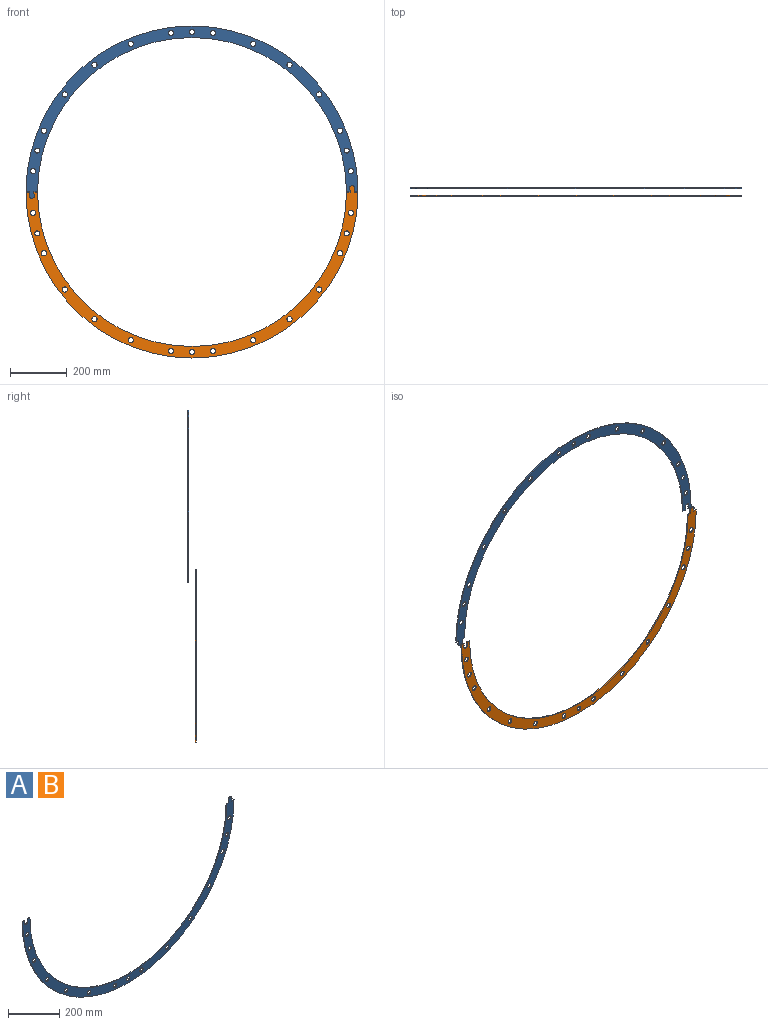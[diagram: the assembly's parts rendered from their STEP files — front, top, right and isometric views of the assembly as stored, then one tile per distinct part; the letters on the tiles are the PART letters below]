
ASSEMBLY  parts=2 mates=1
PART A: 29 faces, bbox 1170.9x3.2x607.7 mm
  f0: plane 12.56x3.18mm, normal (0,0,1), area 39.9mm2, adj f1,f9,f10,f25
  f1: plane 1170.94x607.7mm, normal (0,1,0), area 68201.3mm2, adj f0,f2,f3,f4,f5,f6,f7,f8
  f2: plane 12.84x3.18mm, normal (0,0,1), area 40.8mm2, adj f1,f3,f10,f23
  f3: cylinder r=585.47mm len=1170.94mm, axis (0,1,0), area 5838.2mm2, adj f1,f2,f4,f10
  f4: plane 12.84x3.18mm, normal (0,0,1), area 40.8mm2, adj f1,f3,f5,f10
  f5: plane 7.24x3.18mm, normal (1,0,0), area 23mm2, adj f1,f4,f6,f10
  f6: cylinder r=9.53mm len=19.05mm, axis (0,1,0), area 133.9mm2, adj f1,f5,f7,f10
  f7: plane 7.24x3.18mm, normal (-1,0,0), area 23mm2, adj f1,f6,f8,f10
  f8: plane 12.56x3.18mm, normal (0,0,1), area 39.9mm2, adj f1,f7,f9,f10
  f9: cylinder r=544.83mm len=1089.66mm, axis (0,1,0), area 5432.8mm2, adj f0,f1,f8,f10
  f10: plane 1170.94x607.7mm, normal (0,-1,0), area 68201.3mm2, adj f0,f2,f3,f4,f5,f6,f7,f8
  f11: cylinder r=9.21mm len=18.42mm, axis (0,-1,0), area 183.7mm2, adj f1,f10
  f12: cylinder r=9.21mm len=18.42mm, axis (0,-1,0), area 183.7mm2, adj f1,f10
  f13: cylinder r=9.21mm len=18.42mm, axis (0,-1,0), area 183.7mm2, adj f1,f10
  f14: cylinder r=9.21mm len=18.42mm, axis (0,-1,0), area 183.7mm2, adj f1,f10
  f15: cylinder r=9.21mm len=18.42mm, axis (0,-1,0), area 183.7mm2, adj f1,f10
  f16: cylinder r=9.21mm len=18.42mm, axis (0,-1,0), area 183.7mm2, adj f1,f10
  f17: cylinder r=9.21mm len=18.42mm, axis (0,-1,0), area 183.7mm2, adj f1,f10
  f18: cylinder r=9.21mm len=18.42mm, axis (0,-1,0), area 183.7mm2, adj f1,f10
  f19: cylinder r=9.21mm len=18.42mm, axis (0,-1,0), area 183.7mm2, adj f1,f10
  f20: cylinder r=9.21mm len=18.42mm, axis (0,-1,0), area 183.7mm2, adj f1,f10
  f21: cylinder r=9.21mm len=18.42mm, axis (0,-1,0), area 183.7mm2, adj f1,f10
  f22: cylinder r=9.21mm len=18.42mm, axis (0,-1,0), area 183.7mm2, adj f1,f10
  f23: plane 6.73x3.18mm, normal (1,0,0), area 21.4mm2, adj f1,f2,f10,f24
  f24: cylinder r=9.53mm len=19.05mm, axis (0,-1,0), area 133.9mm2, adj f1,f10,f23,f25
  f25: plane 6.73x3.18mm, normal (-1,0,0), area 21.4mm2, adj f0,f1,f10,f24
  f26: cylinder r=8.89mm len=17.78mm, axis (0,-1,0), area 177.3mm2, adj f1,f10
  f27: cylinder r=8.89mm len=17.78mm, axis (0,-1,0), area 177.3mm2, adj f1,f10
  f28: cylinder r=8.89mm len=17.78mm, axis (0,-1,0), area 177.3mm2, adj f1,f10
PART B: same geometry as A
PLACE A rot(axis=(0,1,0),180deg) t=(-173.56,-240,31.32)mm
PLACE B t=(-173.56,-265.49,31.32)mm fixed
MATE slider B.f6 <-> A.f24  axis (0,-1,0) through (391.45,-268.66,44.02)mm
